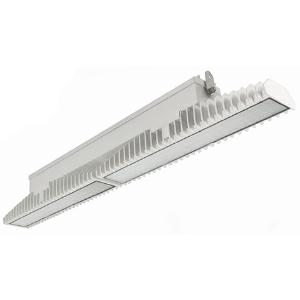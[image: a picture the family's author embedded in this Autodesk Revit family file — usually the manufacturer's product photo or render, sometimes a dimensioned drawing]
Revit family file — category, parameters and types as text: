
# Revit family: 3f_filippi_-_3f_lem_ampio_3f_filippi_-_58885_a0812_-_3f_lem_1_1_led_100_cr_ampio___vs_4830
name_source: partatom
category: Lighting Fixtures
units: mm (PartAtom-declared; Revit-internal decimal feet)

## family parameters
Cut with Voids When Loaded = No
Host = Face
Light Source = No
Part Type = Normal
Room Calculation Point = No
Round Connector Dimension = Use Diameter
Shared = No

## types (1)
- 3F Filippi - 3F LEM Ampio (1 x LED, 13304 lm, 109 W, 4000 K)
    Apparent Load = 109 VA
    Approval mark = CE
    CIE Flux Codes = 67 90 97 100 100
    Color Rendering = 80
    Color Temperature = 4000 K
    Control Gear = Electronic ballast
    Default Elevation = 1800 mm
    Description = Industrial luminaire with high light output and high luminous efficiency designed with the most innovative technologies for environments with temperature up to 55°C.

ILLUMINOTECHNICAL
Luminous efficiency 100% (DLOR 98%, ULOR 2%).
Initial luminous flux of the luminaire 13304 lm.
Direct symmetric wide distribution: the illuminated area has a rectangular shape.
Installation Interdistance Transv.D = 1.24 x hu - Long.D = 1.20 x hu.
Tabular UGR (CIE 117 - 4H-8H; S=0.25H; 70/50/20): RUG 25.8 - 25.6.
Beam angle: 82° - 83°.
Luminous efficacy 122 lm/W.
Lifetime (L93/B10): 30000 h. (tq+25°C)
Lifetime (L90/B10): 50000 h. (tq+25°C)
Lifetime (L85/B10): 80000 h. (tq+25°C)
Lifetime (L80/B10): 100000 h. (tq+25°C)
Lifetime (L85/B10): 50000 h. (tq+55°C)
Sudden decreased luminous flux after 50000 hours: 0% (C0).
Photobiological safety in compliance with IEC/TR 62778: RG0 risk exempt, (IEC 62471).
In compliance with IEC/EN 62722-2-1 - IEC/EN 62717 standards.

SOURCE
2 Mid-Power linear LED modules 50W/840.
Energy efficiency class (UE 2019/2020 - UE 2019/2015): C.
CIE 13.3 Colour rendering index: CRI >80 (R9 <50%).
IES TM-30 Fidelity Index: Rf = 84 Rg = 95.
CCT nominal colour temperature 4000 K.
Colour initial tolerance (MacAdam): SDCM 3.

MECHANICAL
Passive modular heatsinks in die-casted aluminium, painted in white colour.
To optimize the thermal management of the LED module, the heatsinks are oversized and provided with self-cleaning of cooling fins.
Wiring body in aluminium and galvanised steel anchored solidly to the sinks and thermally separated.
3F Lens lenses with high luminous efficiency, transparent methacrylate (PMMA), fixed to the LED modules.
Fixing brackets in stainless steel.
Luminaire with limited surface temperature. - D - (EN 60598-2-24)
Dimensions: 1099x115 mm, height 154 mm. Weight 11.43 kg.
IP65 protection degree.
Mechanical strength to impacts IK06 (1 joule).
Glow-wire test resistance 650°C.

ELECTRICAL
Halogen Free electronic wiring 230V-50/60Hz, power factor 0.97, THD <25%, constant output current, class I, 1 driver.
Power of the luminaire 109 W.
ENEC - CE.
SAFE FLICKER: PstLM=<1 and SVM=<0.4 (IEC TR 61547-1 and IEC TR 63158), to ensure a more comfortable and safe light.
Luminaire compliant with EN 60598-2-22 for power supply from a centralised emergency system CPSS (Central Power Supply System), not incorporated in the luminaire - high risk areas excluded. The default power and flux are 100% in AC and 100% in DC.
Ambient temperature from -30°C to +55°C.
Temperature class T6 max 85°C.
Quick connection via M20 3P connector with 9-13 mm tightening range.
Power unit positioned on a separate compartment by the LED module to ensure optimum temperatures of cabling components, to be inspectable and maintainable.
Relative humidity UR: <85%.

INSTALLATION
Ceiling / Suspended / Wall.
All accessories dedicated to this product are available on the Catalog and on our website www.3F-Filippi.com.

ACCESSORIES
A0812 - Anti-glare microprismatic VS moulded glass, tempered, not flammable, with sealing gasket.
One required for each light module. The pack contains 10 pieces.

APPLICATIONS
In commercial environments, exhibition and industrial areas, stores, open areas.
Applications with high ambient temperature up to 55°C.
Environments in which it is necessary a total protection against falling fragments (eg environments with foodstuffs or machines with moving parts or with extreme temperature changes), use luminaires with polycarbonate lenses.

WARNING
Fixture not suitable for cold stores with an ambient temperature <0°C and/or relative humidity >85%.
Luminaire designed for disposal/recycling at end-of-life.
Replaceable (LED only) light source by a professional. Replaceable control gear by a professional.
    Height = 154 mm
    Lamp = 1 x LED
    Lamp Light Flux = 13304 lm
    Lamp Power = 109 W
    Lamp count = 1
    Length = 1099 mm
    Lifetime = 50000 h
    Luminous efficacy = 122 lm/W
    Manufacturer = 3F Filippi
    ModVariant = No
    Model = 3F Filippi - 58885+A0812 - 3F LEM 1+1 LED 100 CR AMPIO + VS
    Mounting Place = Ceiling
    Mounting Type = Pendant
    Number of Poles = 1
    OnlyDefault = Yes
    Power Factor = 1
    Product Name = 3F Filippi - 3F LEM Ampio
    Product group = pendant luminaire
    ProductGroupID = 9
    Protection Class = Protection class I
    Protection Degree = IP 65
    RLX_Detail_Level = 1
    RLX_Emergency_Light_Flux = 0 lm
    RLX_Emergency_Type = 0
    RLX_Emergency_Type_DB = No
    RlxData = <blob elided: 91129 chars, md5=447859a3>
    Socket = socket
    Standby Power = 0 W
    System Light Flux = 13304 lm
    System Power = 109 W
    Type Comments = Product without accessories
    Type Image = 3f_filippi_-_lem_11__a0812.jpg
    URL = http://relux.com
    VarID = ---
    Voltage = 0 V
    Weight = 0.00 kg
    Width = 115 mm

## geometry (parser evidence)
native form markers: Blend x4, Sweep x12
no freeform markers — native parametric forms only
